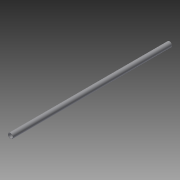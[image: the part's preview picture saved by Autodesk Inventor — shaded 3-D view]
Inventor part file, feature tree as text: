
AUTODESK INVENTOR PART (.ipt)
format: ipt  version: 2015 SP1 (Build 190203100, 203)  size: 69,120 bytes
history: native  units: mm
features: extrude x1, sketch x1
ambient origin geometry x8: Origin, YZ Plane, XZ Plane, XY Plane, X Axis, Y Axis, Z Axis, Center Point
bodies: Solid1 (feature_tree)
feature tree (2):
  extrude  "Extrusion1"  Depth=2200.0mm
  sketch  "Sketch1"  dims[d0=70.0mm d1=62.0mm d2=2200.0mm d3=0.0mm]
